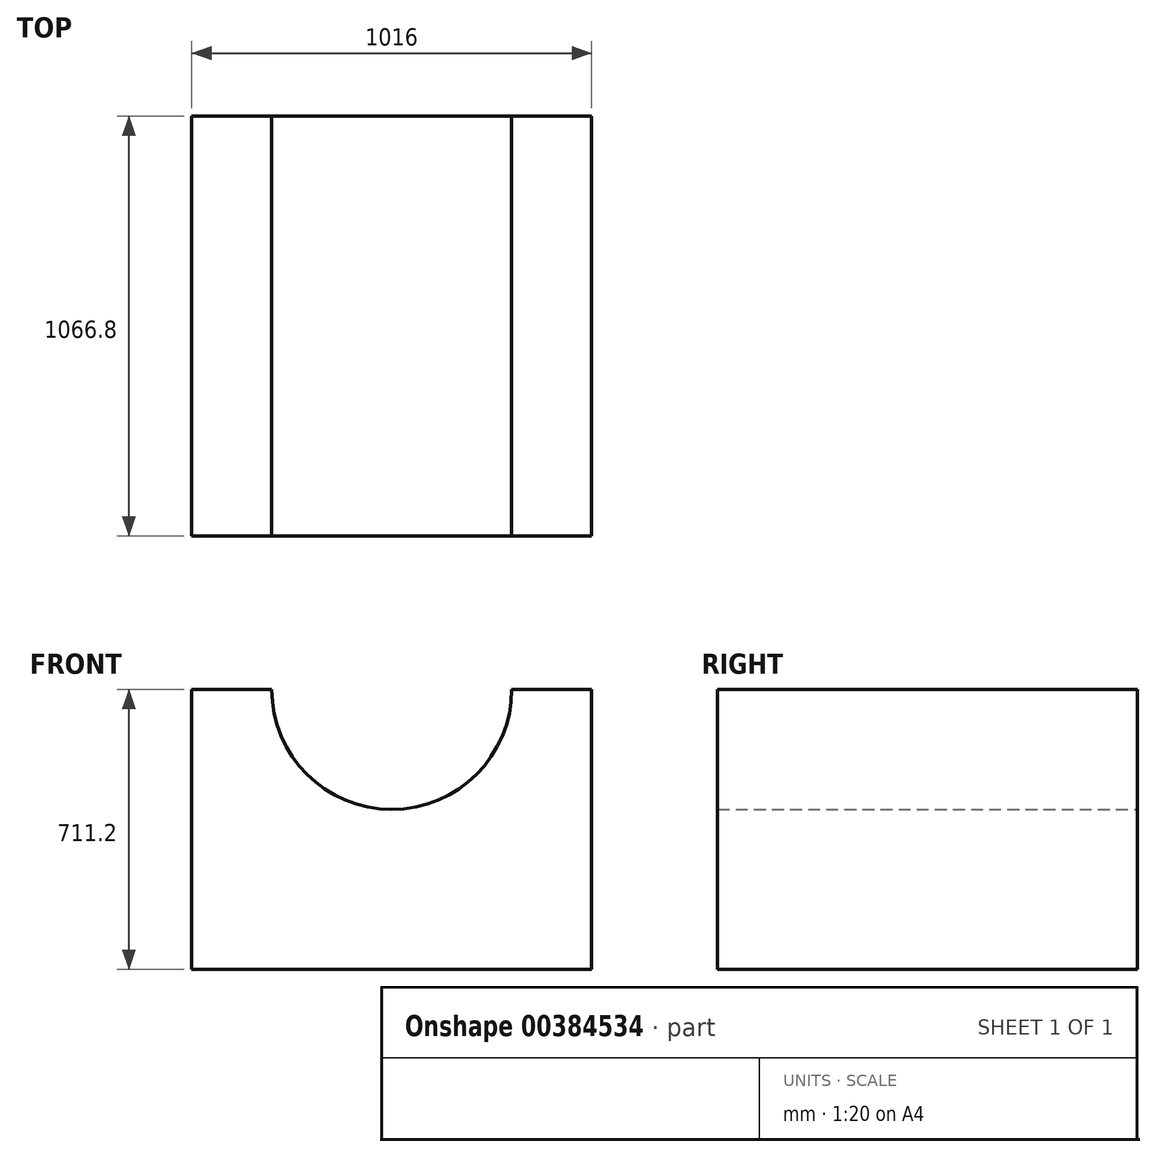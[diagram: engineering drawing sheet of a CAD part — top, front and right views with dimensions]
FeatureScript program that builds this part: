
annotation { "Feature Type Name" : "Feature", "Feature Type Description" : "" }
export const myFeature = defineFeature(function(context is Context, id is Id, definition is map)
    precondition{}
    {
        {
            var Q0;
            Q0=qCreatedBy(makeId("Front.planeOp"),FACE);
            var sketch = newSketch(context, id + "F0", { "sketchPlane" : qUnion([Q0])});
            skLineSegment(sketch, "E0", {"start": v(0, 0) * mm, "end": v(0, 711.2) * mm});
            skLineSegment(sketch, "E1", {"start": v(0, 711.2) * mm, "end": v(203.2, 711.2) * mm});
            skLineSegment(sketch, "E2", {"start": v(1016, 711.2) * mm, "end": v(1016, 0) * mm});
            skLineSegment(sketch, "E3", {"start": v(1016, 0) * mm, "end": v(0, 0) * mm});
            skArc(sketch, "E4", {"start": v(203.2, 711.2) * mm, "mid": v(508, 406.4) * mm, "end": v(812.8, 711.2) * mm});
            skLineSegment(sketch, "E5.trimOffspring", {"start": v(812.8, 711.2) * mm, "end": v(1016, 711.2) * mm});
            skSolve(sketch);
        }
        {
            var Q0;
            Q0 = qSketchRegion(id + "F0", true);
            extrude(context, id + "F1", {"entities" : qUnion([Q0]), "depth" : 1066.8 * mm});
        }
    });
